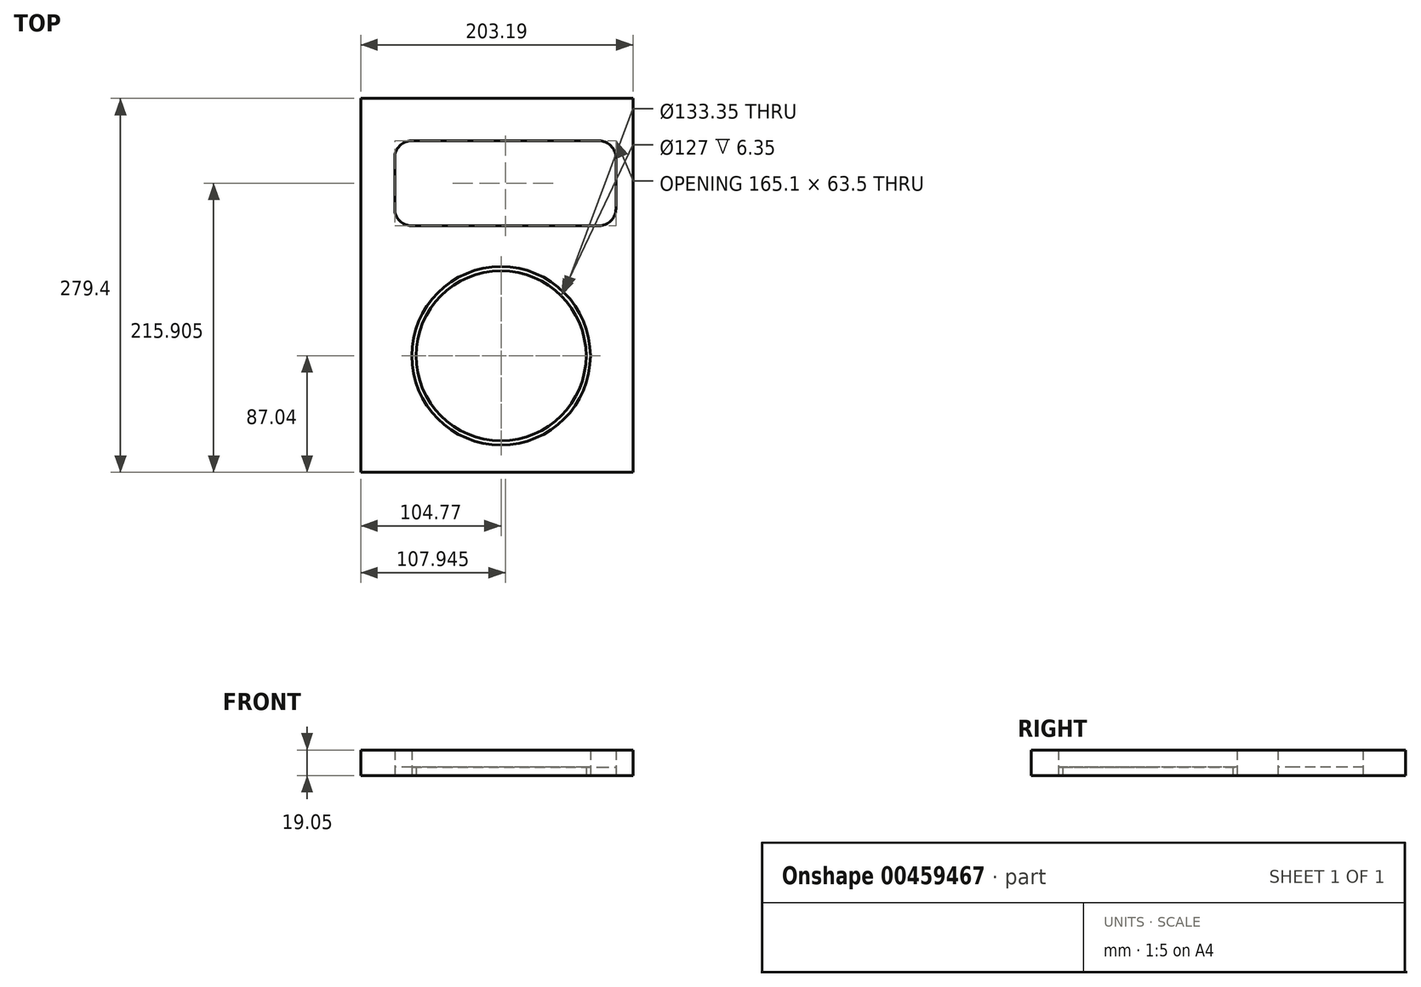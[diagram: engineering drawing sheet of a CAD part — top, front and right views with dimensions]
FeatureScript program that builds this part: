
annotation { "Feature Type Name" : "Feature", "Feature Type Description" : "" }
export const myFeature = defineFeature(function(context is Context, id is Id, definition is map)
    precondition{}
    {
        {
            var Q0;
            Q0=qCreatedBy(makeId("Top.planeOp"),FACE);
            var sketch = newSketch(context, id + "F0", { "sketchPlane" : qUnion([Q0])});
            skCircle(sketch, "E0", {"center": v(0, 0) * mm, "radius": 66.68 * mm});
            skCircle(sketch, "E1", {"center": v(0, 0) * mm, "radius": 63.5 * mm});
            skLineSegment(sketch, "E2.bottom", {"start": v(-104.78, 192.36) * mm, "end": v(98.42, 192.36) * mm});
            skLineSegment(sketch, "E2.top", {"start": v(-104.78, -87.04) * mm, "end": v(98.43, -87.04) * mm});
            skLineSegment(sketch, "E2.left", {"start": v(-104.78, 192.36) * mm, "end": v(-104.78, -87.04) * mm});
            skLineSegment(sketch, "E2.right", {"start": v(98.42, 192.36) * mm, "end": v(98.43, -87.04) * mm});
            skLineSegment(sketch, "E3.bottom", {"start": v(-66.68, 160.61) * mm, "end": v(73.03, 160.61) * mm});
            skLineSegment(sketch, "E3.top", {"start": v(-66.68, 97.11) * mm, "end": v(73.03, 97.11) * mm});
            skLineSegment(sketch, "E3.left", {"start": v(-79.38, 147.91) * mm, "end": v(-79.38, 109.81) * mm});
            skLineSegment(sketch, "E3.right", {"start": v(85.73, 147.91) * mm, "end": v(85.73, 109.81) * mm});
            skPoint(sketch, "E4.visualSharp", {"position": v(-79.38, 160.61) * mm});
            skArc(sketch, "E4.filletArc", {"start": v(-66.68, 160.61) * mm, "mid": v(-75.66, 156.9) * mm, "end": v(-79.38, 147.91) * mm});
            skPoint(sketch, "E5.visualSharp", {"position": v(85.73, 160.61) * mm});
            skArc(sketch, "E5.filletArc", {"start": v(85.73, 147.91) * mm, "mid": v(82, 156.9) * mm, "end": v(73.03, 160.61) * mm});
            skPoint(sketch, "E6.visualSharp", {"position": v(-79.38, 97.11) * mm});
            skArc(sketch, "E6.filletArc", {"start": v(-79.38, 109.81) * mm, "mid": v(-75.66, 100.83) * mm, "end": v(-66.68, 97.11) * mm});
            skPoint(sketch, "E7.visualSharp", {"position": v(85.73, 97.11) * mm});
            skArc(sketch, "E7.filletArc", {"start": v(73.03, 97.11) * mm, "mid": v(82, 100.83) * mm, "end": v(85.73, 109.81) * mm});
            skSolve(sketch);
        }
        {
            var Q0;
            Q0=makeQuery(id+"F0.imprint","IMPRINT",FACE,{"disambiguationData":[TD([[makeQuery(id+"F0.imprint","IMPRINT",EDGE,{"derivedFrom":sQuery(id+"F0.wireOp",EDGE,"E0")}),1.0]])]});
            var Q1;
            Q1=makeQuery(id+"F0.imprint","IMPRINT",FACE,{"disambiguationData":[TD([[makeQuery(id+"F0.imprint","IMPRINT",EDGE,{"derivedFrom":sQuery(id+"F0.wireOp",EDGE,"E3.bottom")}),-1.0]])]});
            extrude(context, id + "F1", {"entities" : qUnion([Q0, Q1]), "depth" : 6.35 * mm});
        }
        {
            var Q0;
            Q0 = qSketchRegion(id + "F0", true);
            extrude(context, id + "F2", {"entities" : qUnion([Q0]), "depth" : 19.05 * mm});
        }
    });
